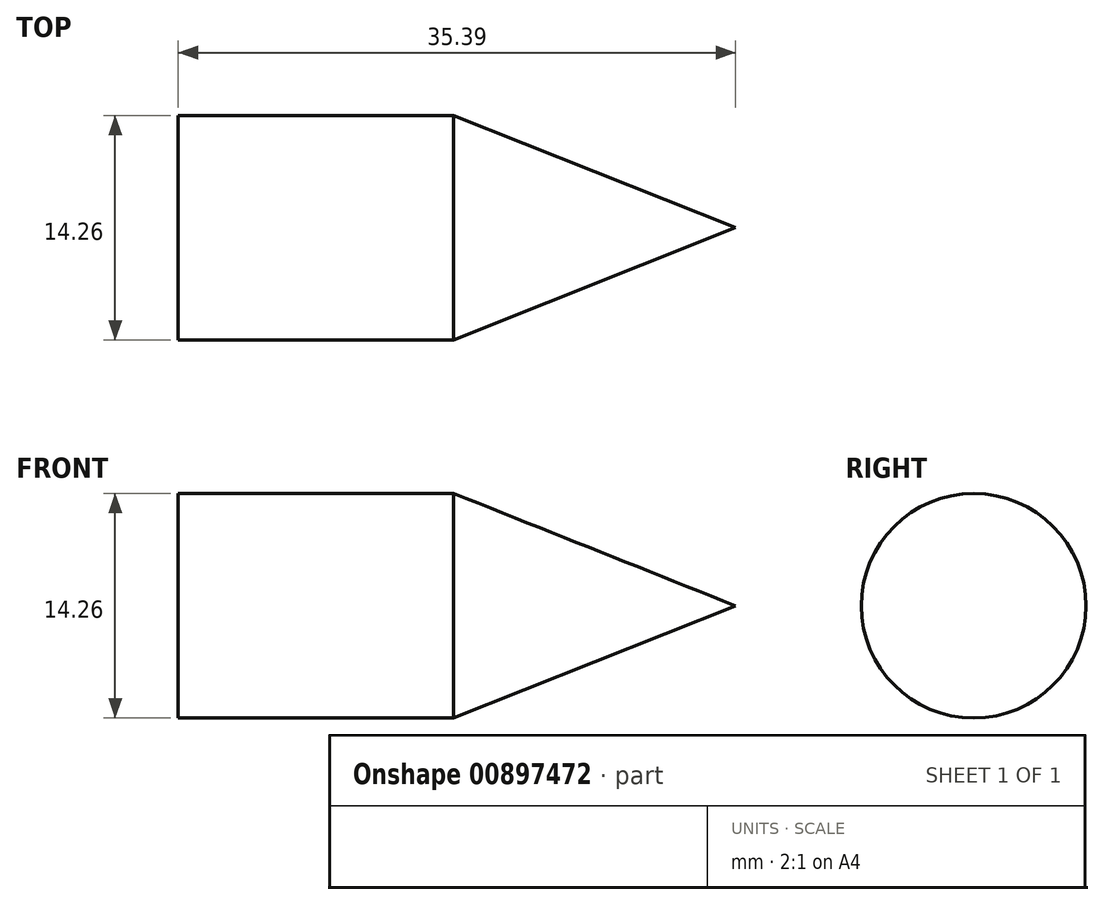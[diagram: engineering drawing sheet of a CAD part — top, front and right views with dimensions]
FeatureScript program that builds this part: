
annotation { "Feature Type Name" : "Feature", "Feature Type Description" : "" }
export const myFeature = defineFeature(function(context is Context, id is Id, definition is map)
    precondition{}
    {
        {
            var Q0;
            Q0=qCreatedBy(makeId("Top.planeOp"),FACE);
            var sketch = newSketch(context, id + "F0", { "sketchPlane" : qUnion([Q0])});
            skLineSegment(sketch, "E0", {"start": v(0, 0) * mm, "end": v(35.39, 0) * mm});
            skLineSegment(sketch, "E1", {"start": v(35.39, 0) * mm, "end": v(17.48, 7.13) * mm});
            skLineSegment(sketch, "E2", {"start": v(17.48, 7.13) * mm, "end": v(0, 7.13) * mm});
            skLineSegment(sketch, "E3", {"start": v(0, 7.13) * mm, "end": v(0, 0) * mm});
            skSolve(sketch);
        }
        {
            var Q0;
            Q0=makeQuery(id+"F0.imprint","IMPRINT",FACE,{"disambiguationData":[TD([[makeQuery(id+"F0.imprint","IMPRINT",EDGE,{"derivedFrom":sQuery(id+"F0.wireOp",EDGE,"E0")}),1.0]])]});
            var Q1;
            Q1=sQuery(id+"F0.wireOp",EDGE,"E0");
            revolve(context, id + "F1", {"surfaceOperationType" : NewSurfaceOperationType.NEW, "entities" : qUnion([Q0]), "axis" : qUnion([Q1]), "revolveType" : RevolveType.FULL});
        }
    });
